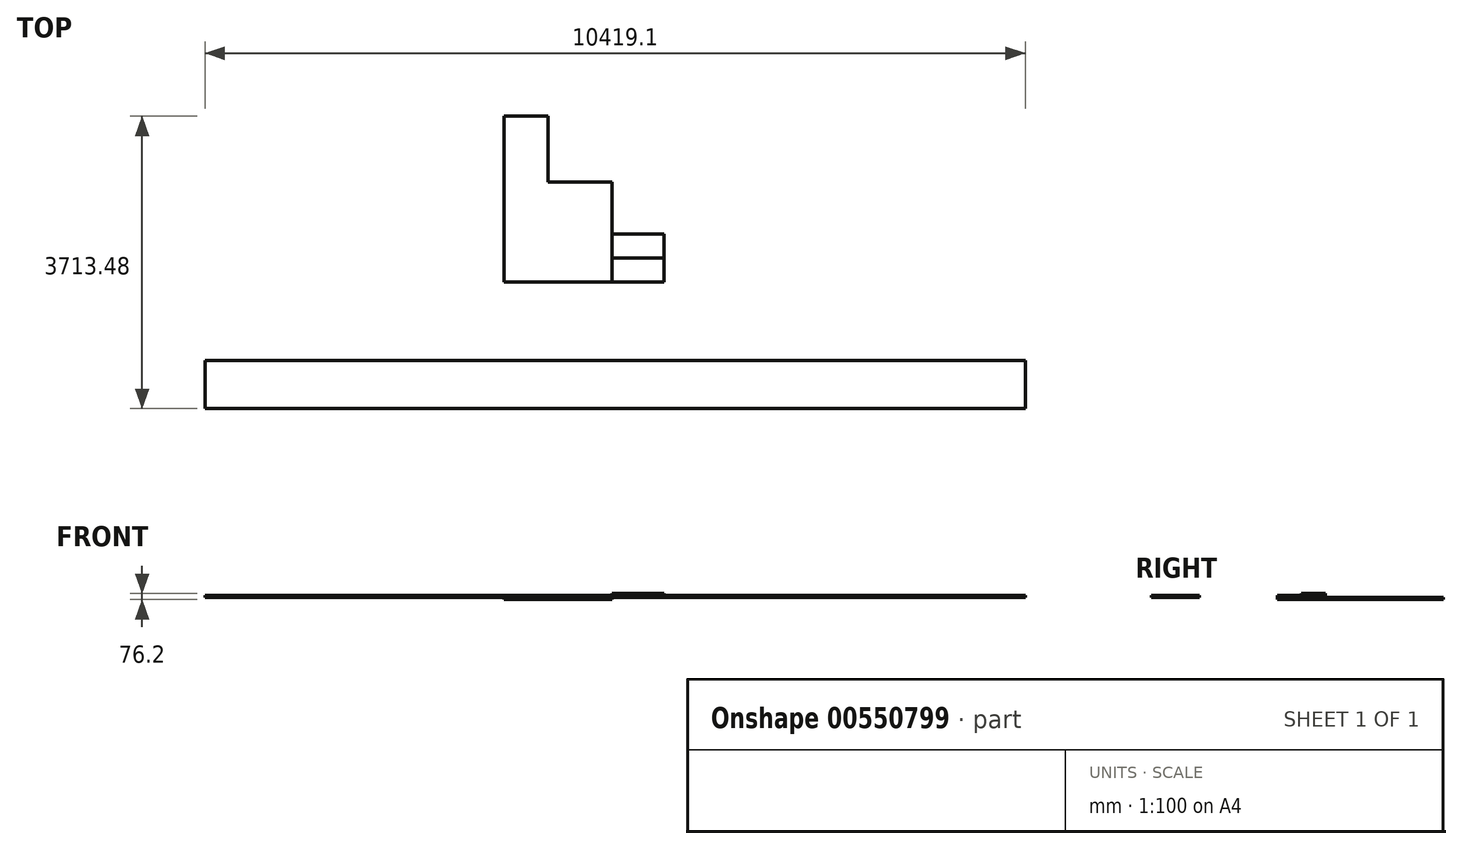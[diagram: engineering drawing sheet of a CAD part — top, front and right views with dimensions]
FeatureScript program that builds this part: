
annotation { "Feature Type Name" : "Feature", "Feature Type Description" : "" }
export const myFeature = defineFeature(function(context is Context, id is Id, definition is map)
    precondition{}
    {
        {
            var Q0;
            Q0=qCreatedBy(makeId("Top.planeOp"),FACE);
            var sketch = newSketch(context, id + "F0", { "sketchPlane" : qUnion([Q0])});
            skLineSegment(sketch, "E0.bottom", {"start": v(0, 0) * mm, "end": v(-812.8, 0) * mm});
            skLineSegment(sketch, "E0.top", {"start": v(0, 1270) * mm, "end": v(-812.8, 1270) * mm});
            skLineSegment(sketch, "E0.left", {"start": v(0, 0) * mm, "end": v(0, 1270) * mm});
            skLineSegment(sketch, "E0.right", {"start": v(-812.8, 0) * mm, "end": v(-812.8, 1270) * mm});
            skLineSegment(sketch, "E1.bottom", {"start": v(-812.8, 0) * mm, "end": v(-1371.6, 0) * mm});
            skLineSegment(sketch, "E1.top", {"start": v(-812.8, 2108.2) * mm, "end": v(-1371.6, 2108.2) * mm});
            skLineSegment(sketch, "E1.left", {"start": v(-812.8, 0) * mm, "end": v(-812.8, 2108.2) * mm});
            skLineSegment(sketch, "E1.right", {"start": v(-1371.6, 0) * mm, "end": v(-1371.6, 2108.2) * mm});
            skSolve(sketch);
        }
        {
            var Q0;
            {var subQ3=sQuery(id+"F0.wireOp",EDGE,"E1.bottom");Q0=makeQuery(id+"F0.imprint","IMPRINT",FACE,{"disambiguationData":[TD([[makeQuery(id+"F0.imprint","IMPRINT",EDGE,{"derivedFrom":subQ3}),-1.0]])]});}
            var Q1;
            {var subQ3=sQuery(id+"F0.wireOp",EDGE,"E0.bottom");Q1=makeQuery(id+"F0.imprint","IMPRINT",FACE,{"disambiguationData":[TD([[makeQuery(id+"F0.imprint","IMPRINT",EDGE,{"derivedFrom":subQ3}),-1.0]])]});}
            var Q2;
            Q2=makeQuery(id+"F0.imprint","IMPRINT",FACE,{"disambiguationData":[TD([[makeQuery(id+"F0.imprint","IMPRINT",EDGE,{"derivedFrom":sQuery(id+"F0.wireOp",EDGE,"yvtz4S72-Cbqx-IxaL-fc4X-qgaAndJ89FCb.bottom")}),-1.0]])]});
            extrude(context, id + "F1", {"entities" : qUnion([Q0, Q1, Q2]), "depth" : 25.4 * mm, "offsetDistance" : 25.4 * mm});
        }
        {
            var Q0;
            Q0=makeQuery(id+"F1.opExtrude","CAP_FACE",FACE,{"disambiguationData":[OSD([sQuery(id+"F0.wireOp",EDGE,"E0.bottom"),sQuery(id+"F0.wireOp",EDGE,"E0.top"),sQuery(id+"F0.wireOp",EDGE,"E0.left"),sQuery(id+"F0.wireOp",EDGE,"E1.bottom"),sQuery(id+"F0.wireOp",EDGE,"E1.top"),sQuery(id+"F0.wireOp",EDGE,"E1.left"),sQuery(id+"F0.wireOp",EDGE,"E1.right"),sQuery(id+"F0.wireOp",EDGE,"yvtz4S72-Cbqx-IxaL-fc4X-qgaAndJ89FCb.bottom"),sQuery(id+"F0.wireOp",EDGE,"yvtz4S72-Cbqx-IxaL-fc4X-qgaAndJ89FCb.top"),sQuery(id+"F0.wireOp",EDGE,"yvtz4S72-Cbqx-IxaL-fc4X-qgaAndJ89FCb.right")])],"isStart":false});
            var sketch = newSketch(context, id + "F2", { "sketchPlane" : qUnion([Q0])});
            skLineSegment(sketch, "E2.left", {"start": v(0, 0) * mm, "end": v(0, 7.07) * mm});
            skLineSegment(sketch, "E3.bottom", {"start": v(0.64, 0) * mm, "end": v(661.04, 0) * mm});
            skLineSegment(sketch, "E3.top", {"start": v(0.63, 304.8) * mm, "end": v(661.04, 304.8) * mm});
            skLineSegment(sketch, "E3.left", {"start": v(0.64, 0) * mm, "end": v(0.64, 304.8) * mm});
            skLineSegment(sketch, "E3.right", {"start": v(661.04, 0) * mm, "end": v(661.04, 304.8) * mm});
            skSolve(sketch);
        }
        {
            var Q0;
            Q0=makeQuery(id+"F2.imprint","IMPRINT",FACE,{"disambiguationData":[TD([[makeQuery(id+"F2.imprint","IMPRINT",EDGE,{"derivedFrom":sQuery(id+"F2.wireOp",EDGE,"E3.bottom")}),1.0]])]});
            extrude(context, id + "F3", {"entities" : qUnion([Q0]), "depth" : 25.4 * mm, "offsetDistance" : 25.4 * mm});
        }
        {
            var Q0;
            Q0=makeQuery(id+"F1.opExtrude","CAP_FACE",FACE,{"disambiguationData":[OSD([sQuery(id+"F0.wireOp",EDGE,"E0.bottom"),sQuery(id+"F0.wireOp",EDGE,"E0.top"),sQuery(id+"F0.wireOp",EDGE,"E0.left"),sQuery(id+"F0.wireOp",EDGE,"E1.bottom"),sQuery(id+"F0.wireOp",EDGE,"E1.top"),sQuery(id+"F0.wireOp",EDGE,"E1.left"),sQuery(id+"F0.wireOp",EDGE,"E1.right"),sQuery(id+"F0.wireOp",EDGE,"yvtz4S72-Cbqx-IxaL-fc4X-qgaAndJ89FCb.bottom"),sQuery(id+"F0.wireOp",EDGE,"yvtz4S72-Cbqx-IxaL-fc4X-qgaAndJ89FCb.top"),sQuery(id+"F0.wireOp",EDGE,"yvtz4S72-Cbqx-IxaL-fc4X-qgaAndJ89FCb.right")])],"isStart":false});
            var sketch = newSketch(context, id + "F4", { "sketchPlane" : qUnion([Q0])});
            skLineSegment(sketch, "E4.bottom", {"start": v(-5170.85, -995.68) * mm, "end": v(5248.27, -995.68) * mm});
            skLineSegment(sketch, "E4.top", {"start": v(-5170.85, -1605.28) * mm, "end": v(5248.27, -1605.28) * mm});
            skLineSegment(sketch, "E4.left", {"start": v(-5170.85, -995.68) * mm, "end": v(-5170.85, -1605.28) * mm});
            skLineSegment(sketch, "E4.right", {"start": v(5248.27, -995.68) * mm, "end": v(5248.27, -1605.28) * mm});
            skSolve(sketch);
        }
        {
            var Q0;
            Q0=makeQuery(id+"F4.imprint","IMPRINT",FACE,{"disambiguationData":[TD([[makeQuery(id+"F4.imprint","IMPRINT",EDGE,{"derivedFrom":sQuery(id+"F4.wireOp",EDGE,"E4.bottom")}),-1.0]])]});
            extrude(context, id + "F5", {"entities" : qUnion([Q0]), "depth" : 25.4 * mm, "offsetDistance" : 25.4 * mm});
        }
        {
            var Q0;
            Q0=makeQuery(id+"F3.opExtrude","CAP_FACE",FACE,{"disambiguationData":[OSD([sQuery(id+"F2.wireOp",EDGE,"E3.bottom"),sQuery(id+"F2.wireOp",EDGE,"E3.top"),sQuery(id+"F2.wireOp",EDGE,"E3.left"),sQuery(id+"F2.wireOp",EDGE,"E3.right")])],"isStart":false});
            var sketch = newSketch(context, id + "F6", { "sketchPlane" : qUnion([Q0])});
            skLineSegment(sketch, "E5.bottom", {"start": v(661.04, 304.8) * mm, "end": v(0, 304.8) * mm});
            skLineSegment(sketch, "E5.top", {"start": v(661.04, 609.6) * mm, "end": v(0, 609.6) * mm});
            skLineSegment(sketch, "E5.left", {"start": v(661.04, 304.8) * mm, "end": v(661.04, 609.6) * mm});
            skLineSegment(sketch, "E5.right", {"start": v(0, 304.8) * mm, "end": v(0, 609.6) * mm});
            skSolve(sketch);
        }
        {
            var Q0;
            Q0=makeQuery(id+"F6.imprint","IMPRINT",FACE,{"disambiguationData":[TD([[makeQuery(id+"F6.imprint","IMPRINT",EDGE,{"derivedFrom":sQuery(id+"F6.wireOp",EDGE,"11Gy5PEn-50P6-4YGW-2zVO-Zmu0b4O6j90C.bottom")}),1.0]])]});
            var Q1;
            Q1=makeQuery(id+"F6.imprint","IMPRINT",FACE,{"disambiguationData":[TD([[makeQuery(id+"F6.imprint","IMPRINT",EDGE,{"derivedFrom":sQuery(id+"F6.wireOp",EDGE,"E5.top")}),1.0]])]});
            extrude(context, id + "F7", {"entities" : qUnion([Q0, Q1]), "depth" : 25.4 * mm, "offsetDistance" : 25.4 * mm});
        }
    });
